# Revit family: DUAL WHITE 2216 IP 65_S2424.SW.1
name_source: partatom
category: Luminarias
units: mm (PartAtom-declared; Revit-internal decimal feet)

## family parameters
Compartido = No
Corte con vacíos al cargar = No
Cota de conector redondo = Diámetro de uso
Origen de luz = Sí
Punto de cálculo de habitación = No
Se basa en plano de trabajo = Sí
Siempre vertical = No
Tipo de pieza = Normal

## types (1)
- DUAL WHITE 2216 IP 65_S2424.SW.1
    Ancho = 8 mm  [stored 0.0262467 ft]
    Cambio de temperatura de color de luz atenuada = <Ninguno>
    Comentarios de vataje = 24V
    Costo = 0 $
    Descripción = TIRA LED DUAL WHITE 8MM DE ANCHO IP65 USO PARA INTERIORES COMO PARA EXTERIORES, DE PCB BLANCO CON RECUBRIMIENTO, TONO AJUSTABLE DE TRES HILOS Y BANDA DE ALTA INTENSIDAD, CON UNA POTENCIA DE 19.2W/M DE UN TIPO DE LED 2216 SMD, IRC90, 240 LEDS POR METRO, PRESENTACION DE 5M, TEMPERATURA DESDE BLANCO CALIDO A BLANCO FRIO 2700-6000K, 1300 LUMENES POR METRO, EFICIENCIA DE 80 LM/W, CORTE A 5CM, ALIMENTADA A 24V, REQUIERE ACCESORIOS COMO: FUENTE DE PODER Y CABLE DE ALIMENTACION. PERFIL PARA SOBREPONER, SPLIT BOX, CONTROL PARA ATENUAR TIRA, CONTROLADOR DMX, Y MEMORIA PARA ESCENAS/CONTROL.
    Elevación por defecto = 0 mm  [stored 0 ft]
    Fabricante = BRILLANT
    Filtro de color = 16777215
    Longitud de línea de emisión = 600 mm  [stored 1.9685 ft]
    Longitud de símbolo de origen de luz = 1500 mm  [stored 4.92126 ft]
    Lámpara = 2216 SMD
    Modelo = S2424.SW.1
    Ángulo de campo de foco = 90.00°
    Ángulo de enfoque = 30.00°
    Ángulo de inclinación = 60.00°

note: [stored X ft] marks values corroborated as IEEE doubles in the binary element streams (Revit-internal decimal feet)

## geometry (parser evidence)
native form markers: Blend x2
no freeform markers — native parametric forms only
